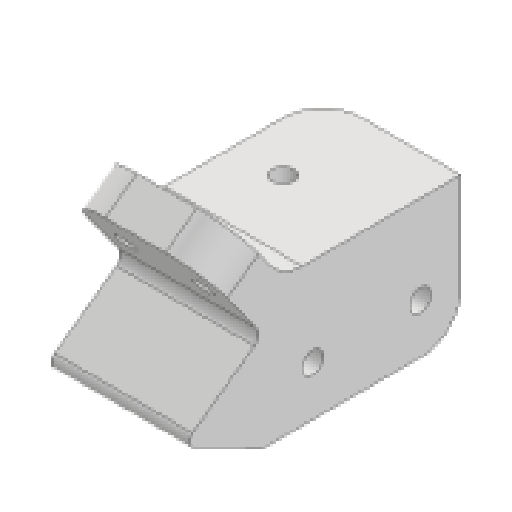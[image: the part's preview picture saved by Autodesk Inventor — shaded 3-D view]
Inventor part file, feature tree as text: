
AUTODESK INVENTOR PART (.ipt)
format: ipt  version: 2025 (Build 290162000, 162)  size: 209,920 bytes
history: native  units: mm
features: reference x6, extrude x4, sketch x4, projected_geometry x4, fillet x3, other x3, mirror x1
ambient origin geometry x8: Origin, YZ Plane, XZ Plane, XY Plane, X Axis, Y Axis, Z Axis, Center Point
bodies: Solid1 (feature_tree)
feature tree (25):
  extrude  "Extrusion1"  Depth=50.8mm
  extrude  "Extrusion2"  Depth=5.5mm
  extrude  "Extrusion3"  Depth=10.0mm
  extrude  "Extrusion4"  Depth=10.0mm
  fillet  "Fillet1"  Radius=5.5mm
  fillet  "Fillet2"  Radius=35.4mm
  fillet  "Fillet3"  Radius=2.6mm
  mirror  "Mirror1"
  sketch  "Sketch1"  dims[d0=25.4mm d1=50.8mm]
  sketch  "Sketch2"  dims[d2=5.5mm d3=5.5mm]
  projected_geometry  "Projected Loop1"
  reference  "Reference1"
  reference  "Reference2"
  reference  "Reference3"
  reference  "Reference4"
  reference  "Reference5"
  reference  "Reference6"
  sketch  "Sketch3"  dims[d4=10.0mm d5=0.0mm d6=10.0mm]
  projected_geometry  "Projected Loop2"
  projected_geometry  "Projected Loop3"
  projected_geometry  "Projected Loop4"
  sketch  "Sketch4"  dims[d7=35.4mm d8=0.0mm d9=10.0mm d10=5.5mm d11=35.4mm d12=0.0mm d13=2.6mm d14=20.0mm d15=35.4mm d16=0.0mm d17=10.0mm d18=10.0mm d19=2.0mm]
  other  "<userpath>\Desktop\puppycat\woodhouseMK1.iam"
  other  "woodhouseMK1.iam"
  other  "horizontalStrutLower:2"
